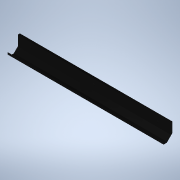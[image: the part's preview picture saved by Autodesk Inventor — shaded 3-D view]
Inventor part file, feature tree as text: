
AUTODESK INVENTOR PART (.ipt)
format: ipt  version: 2022 (Build 260153000, 153)  size: 139,264 bytes
history: native  units: in
note: dims shown in document units (in); Inventor stores cm internally (conversion verified against a paired STEP export)
features: sketch x2, extrude x1, hole x1, direct_edit x1, revolve x1
ambient origin geometry x8: Origin, YZ Plane, XZ Plane, XY Plane, X Axis, Y Axis, Z Axis, Center Point
bodies: Solid1 (feature_tree)
feature tree (6):
  extrude  "Extrusion1"  Depth=0.1575in
  hole  "Hole1"  [1 undecoded]
  direct_edit  "Direct Edit1"
  sketch  "Sketch1"  dims[d0=0.7874in d1=0.1575in]
  sketch  "Sketch2"  dims[d6=11.811in d7=0.0in d8=135.0deg d11=0.7874in d12=0.315in d13=0.1114in d14=0.1114in d15=0.3937in d16=0.9843in d17=0.1339in d18=0.2362in d19=0.2559in d20=0.0394in d21=90.0deg d22=0.315in d23=0.8108in d24=90.0deg]
  revolve  "Rotate1"  [1 undecoded]
note: 2 required parameter values undecoded (feature->parameter linkage not recoverable at this tier; creation-order binding heuristic only, values carry confidence <= 0.55)